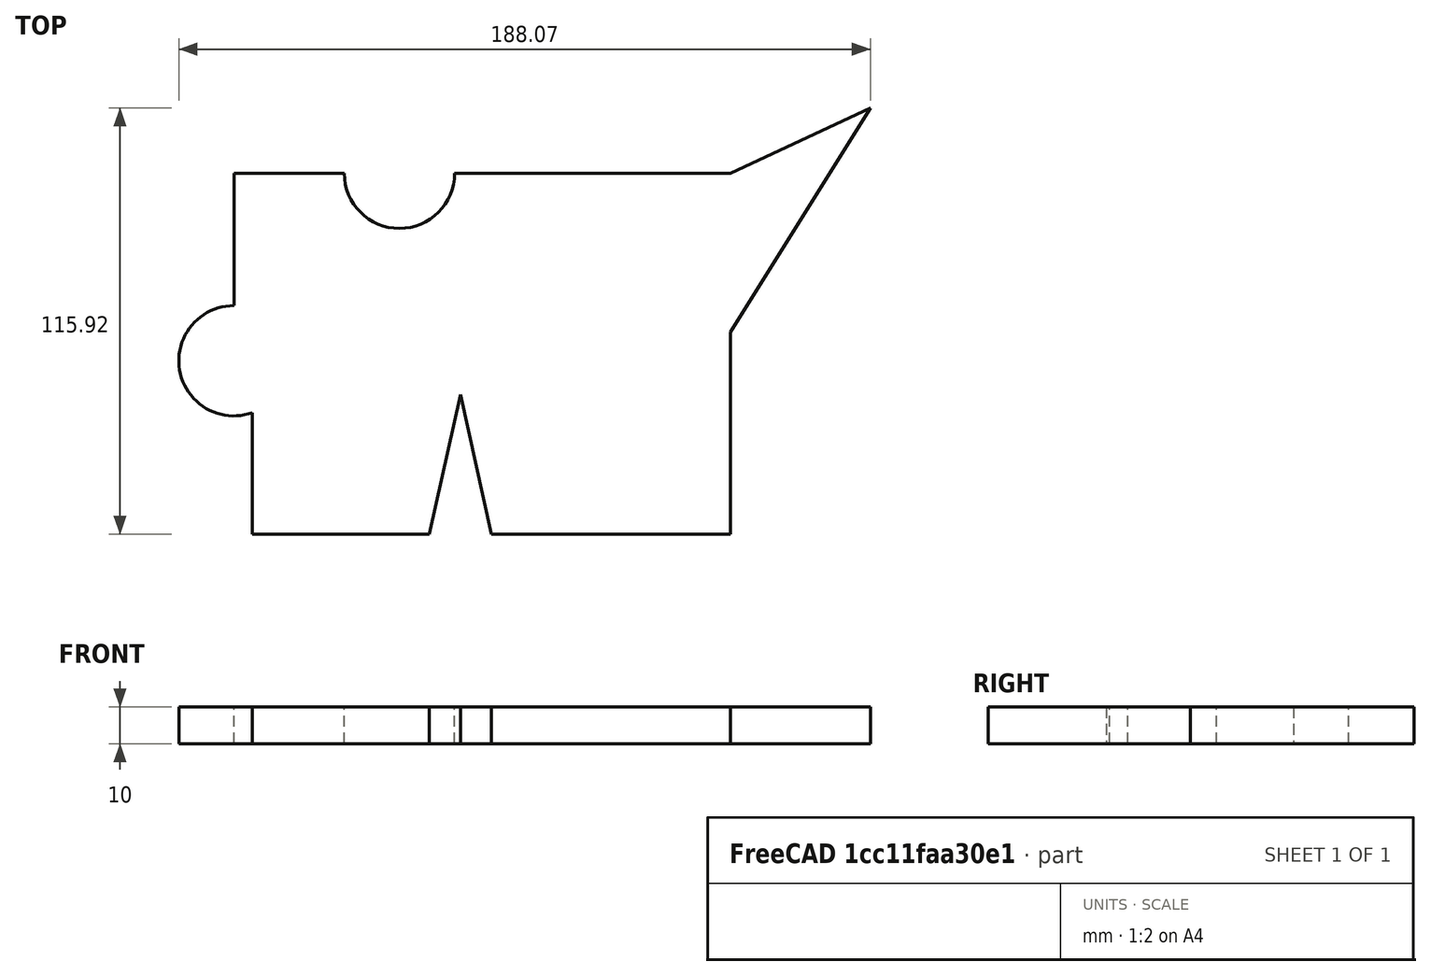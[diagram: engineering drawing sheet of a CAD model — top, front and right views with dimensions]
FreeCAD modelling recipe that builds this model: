
FCSTD DOCUMENT  (FreeCAD 0.19R16149 (Git))
Label: Profile1
License: CreativeCommons Attribution
LicenseURL: http://creativecommons.org/licenses/by/4.0/
objects: Sketcher::SketchObject×1, PartDesign::Pad×1, PartDesign::Body×1
note: 4 computed .brp shape members not serialized (recipe doc carries the construction recipe); baked Part::Feature solids carry a one-line shape summary decoded from their .brp

FEATURE [Sketcher::SketchObject] Sketch
  MapMode = 5
  Support = -> [XY_Plane]
  sketch-geometry (13):
    g0: LineSegment StartX=111.489 StartY=77.9166 StartZ=0 EndX=73.4244 EndY=60.1667 EndZ=0
    g1: LineSegment StartX=73.4244 StartY=60.1667 StartZ=0 EndX=-1.5756 EndY=60.1667 EndZ=0
    g2: ArcOfCircle CenterX=-16.5756 CenterY=60.1667 CenterZ=0 NormalX=0 NormalY=0 NormalZ=1 AngleXU=0 Radius=15 StartAngle=3.14159 EndAngle=6.28319
    g3: LineSegment StartX=-31.5756 StartY=60.1667 StartZ=0 EndX=-61.5756 EndY=60.1667 EndZ=0
    g4: LineSegment StartX=-61.5756 StartY=60.1667 StartZ=0 EndX=-61.5756 EndY=24.1667 EndZ=0
    g5: ArcOfCircle CenterX=-61.5756 CenterY=9.16665 CenterZ=0 NormalX=0 NormalY=0 NormalZ=1 AngleXU=0 Radius=15 StartAngle=1.5708 EndAngle=5.05223
    g6: LineSegment StartX=-56.5756 StartY=-4.97549 StartZ=0 EndX=-56.5756 EndY=-38 EndZ=0
    g7: LineSegment StartX=-56.5756 StartY=-38 StartZ=0 EndX=-8.4244 EndY=-38 EndZ=0
    g8: LineSegment StartX=-8.4244 StartY=-38 StartZ=0 EndX=0 EndY=0 EndZ=0
    g9: LineSegment StartX=0 StartY=0 StartZ=0 EndX=8.4244 EndY=-38 EndZ=0
    g10: LineSegment StartX=8.4244 StartY=-38 StartZ=0 EndX=73.4244 EndY=-38 EndZ=0
    g11: LineSegment StartX=73.4244 StartY=-38 StartZ=0 EndX=73.4244 EndY=17 EndZ=0
    g12: LineSegment StartX=73.4244 StartY=17 StartZ=0 EndX=111.489 EndY=77.9166 EndZ=0
  constraints (37):
    c: Coincident(g0,g1)
    c: Horizontal(g1)
    c: Perpendicular(g1,g2) = 4.71239
    c: Perpendicular(g2,g3) = 4.71239
    c: Coincident(g3,g4)
    c: Vertical(g4)
    c: Perpendicular(g4,g5) = 4.71239
    c: Coincident(g5,g6)
    c: Coincident(g6,g7)
    c: Horizontal(g7)
    c: Coincident(g7,g8)
    c: Coincident(g8,g9)
    c: Coincident(g9,g10)
    c: Horizontal(g10)
    c: Coincident(g10,g11)
    c: Vertical(g11)
    c: Coincident(g11,g12)
    c: Coincident(g12,g0)
    c: Equal(g2,g5)
    c: Horizontal(g3)
    c: PointOnObject(g0,g11)
    c: Equal(g9,g8)
    c: PointOnObject(g7,g10)
    c: Vertical(g6)
    c: DistanceX(g3,g0) = 135
    c: DistanceX(g4,g5) = 5
    c: Radius(g2) = 15
    c: DistanceY(g9,g9) = 38
    c: DistanceX(g10,g10) = 65
    c: Angle(g8,g9) = 0.436332
    c: Angle(g0,g12) = 0.575959
    c: Angle(g0,g1) = 2.70526
    c: DistanceX(g3,g3) = 30
    c: DistanceY(g4,g4) = 36
    c: Distance(g0) = 42
    c: Coincident(g8,g-1)
    c: DistanceY(g11,g11) = 55
FEATURE [PartDesign::Pad] Pad
  Length = 10
  Length2 = 100
  Profile = -> Sketch
  Type = 0
FEATURE [PartDesign::Body] Body  label="Profile1"
  Group = -> [Sketch,Pad]
  Origin = -> Origin
  Tip = -> Pad
